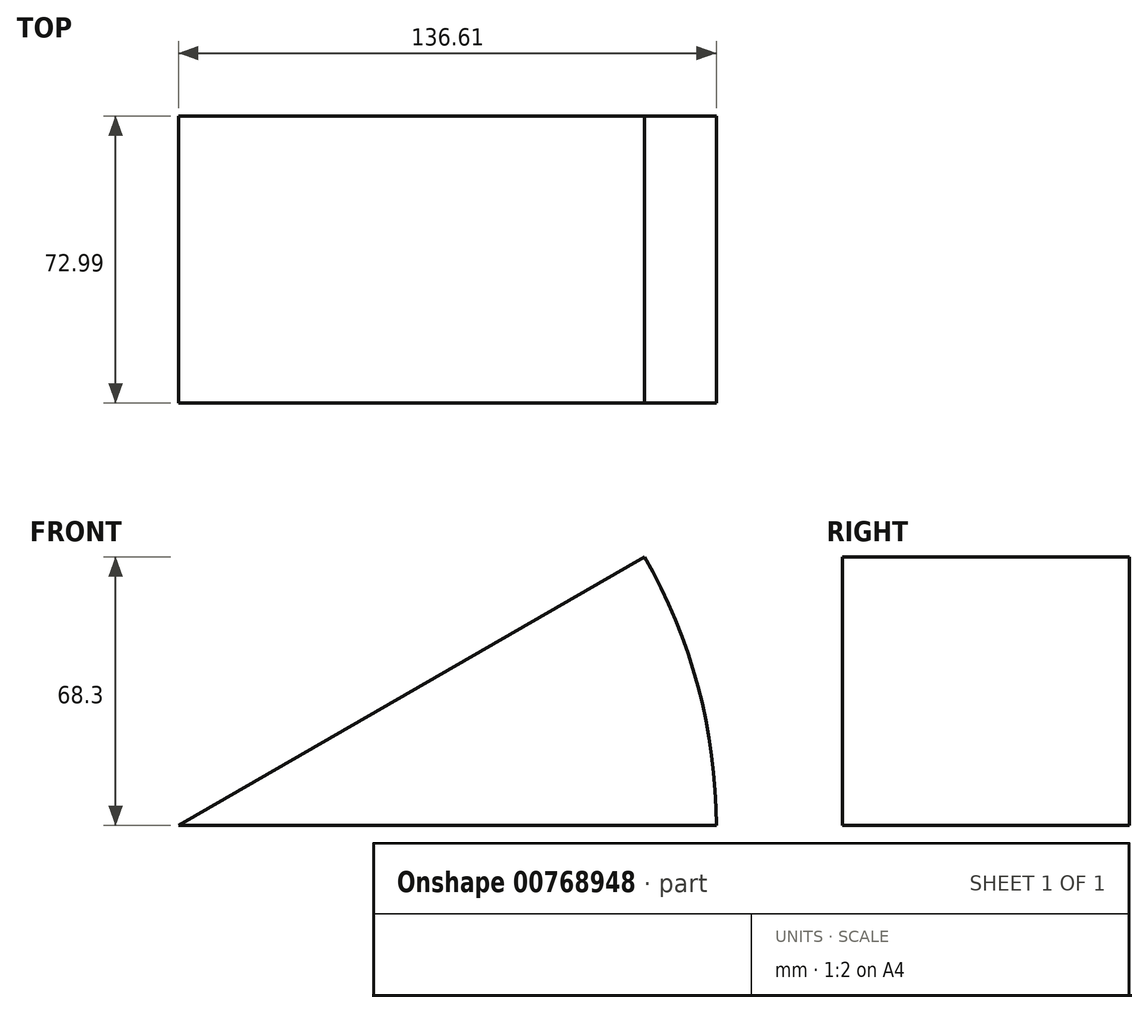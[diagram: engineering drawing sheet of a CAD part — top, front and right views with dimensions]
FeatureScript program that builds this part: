
annotation { "Feature Type Name" : "Feature", "Feature Type Description" : "" }
export const myFeature = defineFeature(function(context is Context, id is Id, definition is map)
    precondition{}
    {
        {
            var Q0;
            Q0=qCreatedBy(makeId("Top.planeOp"),FACE);
            var sketch = newSketch(context, id + "F0", { "sketchPlane" : qUnion([Q0])});
            skLineSegment(sketch, "E0.bottom", {"start": v(0, 0) * mm, "end": v(136.6, 0) * mm});
            skLineSegment(sketch, "E0.top", {"start": v(0, -73) * mm, "end": v(136.6, -73) * mm});
            skLineSegment(sketch, "E0.left", {"start": v(0, 0) * mm, "end": v(0, -73) * mm});
            skLineSegment(sketch, "E0.right", {"start": v(136.6, 0) * mm, "end": v(136.6, -73) * mm});
            skSolve(sketch);
        }
        {
            var Q0;
            Q0=makeQuery(id+"F0.imprint","IMPRINT",FACE,{"disambiguationData":[TD([[makeQuery(id+"F0.imprint","IMPRINT",EDGE,{"derivedFrom":sQuery(id+"F0.wireOp",EDGE,"E0.bottom")}),-1.0]])]});
            var Q1;
            Q1=sQuery(id+"F0.wireOp",EDGE,"E0.left");
            revolve(context, id + "F1", {"surfaceOperationType" : NewSurfaceOperationType.NEW, "entities" : qUnion([Q0]), "axis" : qUnion([Q1]), "revolveType" : RevolveType.ONE_DIRECTION, "angle" : 30 * degree});
        }
    });
